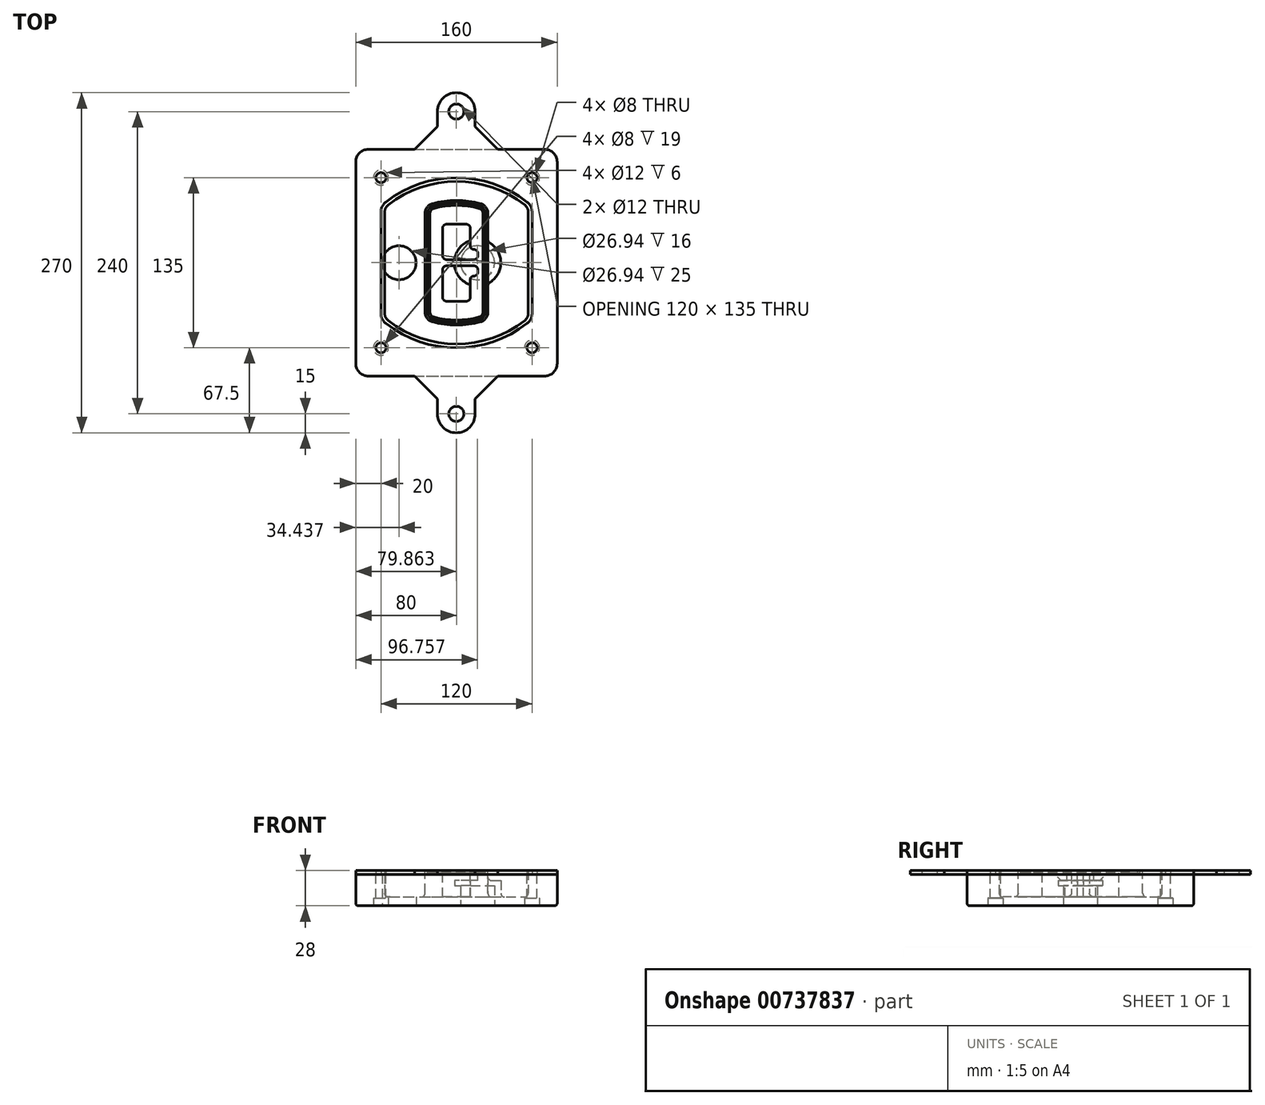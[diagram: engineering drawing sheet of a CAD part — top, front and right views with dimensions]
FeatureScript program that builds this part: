
annotation { "Feature Type Name" : "Feature", "Feature Type Description" : "" }
export const myFeature = defineFeature(function(context is Context, id is Id, definition is map)
    precondition{}
    {
        {
            var Q0;
            Q0=qCreatedBy(makeId("Top.planeOp"),FACE);
            var sketch = newSketch(context, id + "F0", { "sketchPlane" : qUnion([Q0])});
            skPoint(sketch, "E0.rect.middle", {"position": v(0, 0) * mm});
            skLineSegment(sketch, "E1.bottom", {"start": v(-70, -90) * mm, "end": v(70, -90) * mm});
            skLineSegment(sketch, "E1.top", {"start": v(-70, 90) * mm, "end": v(70, 90) * mm});
            skLineSegment(sketch, "E1.left", {"start": v(-80, -80) * mm, "end": v(-80, 80) * mm});
            skLineSegment(sketch, "E1.right", {"start": v(80, -80) * mm, "end": v(80, 80) * mm});
            skLineSegment(sketch, "E2", {"start": v(-80, 90) * mm, "end": v(80, -90) * mm, "construction": true});
            skLineSegment(sketch, "E3", {"start": v(80, 90) * mm, "end": v(-80, -90) * mm, "construction": true});
            skCircle(sketch, "E4", {"center": v(-60, 67.5) * mm, "radius": 4 * mm});
            skCircle(sketch, "E5", {"center": v(60, 67.5) * mm, "radius": 4 * mm});
            skCircle(sketch, "E6", {"center": v(60, -67.5) * mm, "radius": 4 * mm});
            skCircle(sketch, "E7", {"center": v(-60, -67.5) * mm, "radius": 4 * mm});
            skLineSegment(sketch, "E8", {"start": v(-60, 67.5) * mm, "end": v(60, 67.5) * mm, "construction": true});
            skLineSegment(sketch, "E9", {"start": v(60, 67.5) * mm, "end": v(60, -67.5) * mm, "construction": true});
            skLineSegment(sketch, "E10", {"start": v(60, -67.5) * mm, "end": v(-60, -67.5) * mm, "construction": true});
            skLineSegment(sketch, "E11", {"start": v(-60, -67.5) * mm, "end": v(-60, 67.5) * mm, "construction": true});
            skLineSegment(sketch, "E12", {"start": v(-60, 40.3) * mm, "end": v(-60, -40.3) * mm});
            skLineSegment(sketch, "E13", {"start": v(60, 40.3) * mm, "end": v(60, -40.3) * mm});
            skArc(sketch, "E14", {"start": v(56.15, 48.18) * mm, "mid": v(0, 67.5) * mm, "end": v(-56.15, 48.18) * mm});
            skArc(sketch, "E15", {"start": v(-56.15, -48.18) * mm, "mid": v(0, -67.5) * mm, "end": v(56.15, -48.18) * mm});
            skLineSegment(sketch, "E16", {"start": v(-60, 0) * mm, "end": v(60, 0) * mm, "construction": true});
            skPoint(sketch, "E17.visualSharp", {"position": v(-60, -45) * mm});
            skArc(sketch, "E17.filletArc", {"start": v(-60, -40.3) * mm, "mid": v(-58.99, -44.68) * mm, "end": v(-56.15, -48.18) * mm});
            skPoint(sketch, "E18.visualSharp", {"position": v(-60, 45) * mm});
            skArc(sketch, "E18.filletArc", {"start": v(-56.15, 48.18) * mm, "mid": v(-58.99, 44.68) * mm, "end": v(-60, 40.3) * mm});
            skPoint(sketch, "E19.visualSharp", {"position": v(60, 45) * mm});
            skArc(sketch, "E19.filletArc", {"start": v(60, 40.3) * mm, "mid": v(58.99, 44.68) * mm, "end": v(56.15, 48.18) * mm});
            skPoint(sketch, "E20.visualSharp", {"position": v(60, -45) * mm});
            skArc(sketch, "E20.filletArc", {"start": v(56.15, -48.18) * mm, "mid": v(58.99, -44.68) * mm, "end": v(60, -40.3) * mm});
            skPoint(sketch, "E21.visualSharp", {"position": v(-80, 90) * mm});
            skArc(sketch, "E21.filletArc", {"start": v(-70, 90) * mm, "mid": v(-77.07, 87.07) * mm, "end": v(-80, 80) * mm});
            skPoint(sketch, "E22.visualSharp", {"position": v(80, 90) * mm});
            skArc(sketch, "E22.filletArc", {"start": v(80, 80) * mm, "mid": v(77.07, 87.07) * mm, "end": v(70, 90) * mm});
            skPoint(sketch, "E23.visualSharp", {"position": v(80, -90) * mm});
            skArc(sketch, "E23.filletArc", {"start": v(70, -90) * mm, "mid": v(77.07, -87.07) * mm, "end": v(80, -80) * mm});
            skPoint(sketch, "E24.visualSharp", {"position": v(-80, -90) * mm});
            skArc(sketch, "E24.filletArc", {"start": v(-80, -80) * mm, "mid": v(-77.07, -87.07) * mm, "end": v(-70, -90) * mm});
            skArc(sketch, "E25.0", {"start": v(57, 40.3) * mm, "mid": v(56.3, 43.36) * mm, "end": v(54.3, 45.81) * mm});
            skLineSegment(sketch, "E25.1", {"start": v(57, 40.3) * mm, "end": v(57, -40.3) * mm});
            skArc(sketch, "E25.2", {"start": v(54.3, -45.81) * mm, "mid": v(56.3, -43.36) * mm, "end": v(57, -40.3) * mm});
            skArc(sketch, "E25.3", {"start": v(-54.3, -45.81) * mm, "mid": v(0, -64.5) * mm, "end": v(54.3, -45.81) * mm});
            skArc(sketch, "E25.4", {"start": v(-57, -40.3) * mm, "mid": v(-56.3, -43.36) * mm, "end": v(-54.3, -45.81) * mm});
            skArc(sketch, "E25.5", {"start": v(54.3, 45.81) * mm, "mid": v(0, 64.5) * mm, "end": v(-54.3, 45.81) * mm});
            skLineSegment(sketch, "E25.6", {"start": v(-57, 40.3) * mm, "end": v(-57, -40.3) * mm});
            skArc(sketch, "E25.7", {"start": v(-54.3, 45.81) * mm, "mid": v(-56.3, 43.36) * mm, "end": v(-57, 40.3) * mm});
            skArc(sketch, "E26.0", {"start": v(-58.62, 51.33) * mm, "mid": v(-62.58, 46.43) * mm, "end": v(-64, 40.3) * mm});
            skArc(sketch, "E26.1", {"start": v(58.62, 51.33) * mm, "mid": v(0, 71.5) * mm, "end": v(-58.62, 51.33) * mm});
            skArc(sketch, "E26.2", {"start": v(64, 40.3) * mm, "mid": v(62.58, 46.43) * mm, "end": v(58.62, 51.33) * mm});
            skLineSegment(sketch, "E26.3", {"start": v(64, 40.3) * mm, "end": v(64, -40.3) * mm});
            skArc(sketch, "E26.4", {"start": v(58.62, -51.33) * mm, "mid": v(62.58, -46.43) * mm, "end": v(64, -40.3) * mm});
            skLineSegment(sketch, "E26.5", {"start": v(-64, 40.3) * mm, "end": v(-64, -40.3) * mm});
            skArc(sketch, "E26.6", {"start": v(-58.62, -51.33) * mm, "mid": v(0, -71.5) * mm, "end": v(58.62, -51.33) * mm});
            skArc(sketch, "E26.7", {"start": v(-64, -40.3) * mm, "mid": v(-62.58, -46.43) * mm, "end": v(-58.62, -51.33) * mm});
            skPoint(sketch, "E27.startSnap0", {"position": v(0, 90) * mm});
            skLineSegment(sketch, "E28", {"start": v(0, 90) * mm, "end": v(0, 120) * mm, "construction": true});
            skSolve(sketch);
        }
        {
            var Q0;
            Q0=makeQuery(id+"F0.imprint","IMPRINT",FACE,{"disambiguationData":[TD([[makeQuery(id+"F0.imprint","IMPRINT",EDGE,{"derivedFrom":sQuery(id+"F0.wireOp",EDGE,"E1.bottom")}),1.0]])]});
            var Q1;
            Q1=makeQuery(id+"F0.imprint","IMPRINT",FACE,{"disambiguationData":[TD([[makeQuery(id+"F0.imprint","IMPRINT",EDGE,{"derivedFrom":sQuery(id+"F0.wireOp",EDGE,"E12")}),1.0]])]});
            var Q2;
            Q2=makeQuery(id+"F0.imprint","IMPRINT",FACE,{"disambiguationData":[TD([[makeQuery(id+"F0.imprint","IMPRINT",EDGE,{"derivedFrom":sQuery(id+"F0.wireOp",EDGE,"E25.0")}),1.0]])]});
            var Q3;
            Q3=makeQuery(id+"F0.imprint","IMPRINT",FACE,{"disambiguationData":[TD([[makeQuery(id+"F0.imprint","IMPRINT",EDGE,{"derivedFrom":sQuery(id+"F0.wireOp",EDGE,"E12")}),-1.0]])]});
            extrude(context, id + "F1", {"entities" : qUnion([Q0, Q1, Q2, Q3]), "oppositeDirection" : true, "depth" : 25 * mm});
        }
        {
            var Q0;
            Q0=makeQuery(id+"F0.imprint","IMPRINT",FACE,{"disambiguationData":[TD([[makeQuery(id+"F0.imprint","IMPRINT",EDGE,{"derivedFrom":sQuery(id+"F0.wireOp",EDGE,"E12")}),1.0]])]});
            extrude(context, id + "F2", {"entities" : qUnion([Q0]), "operationType" : NewBodyOperationType.ADD, "depth" : 3 * mm});
        }
        {
            var Q0;
            Q0=makeQuery(id+"F0.imprint","IMPRINT",FACE,{"disambiguationData":[TD([[makeQuery(id+"F0.imprint","IMPRINT",EDGE,{"derivedFrom":sQuery(id+"F0.wireOp",EDGE,"E25.0")}),1.0]])]});
            extrude(context, id + "F3", {"entities" : qUnion([Q0]), "operationType" : NewBodyOperationType.REMOVE, "oppositeDirection" : true, "depth" : 18 * mm});
        }
        {
            var Q0;
            Q0=makeQuery(id+"F2.opExtrude","CAP_FACE",FACE,{"disambiguationData":[OSD([sQuery(id+"F0.wireOp",EDGE,"E12"),sQuery(id+"F0.wireOp",EDGE,"E13"),sQuery(id+"F0.wireOp",EDGE,"E14"),sQuery(id+"F0.wireOp",EDGE,"E15"),sQuery(id+"F0.wireOp",EDGE,"E17.filletArc"),sQuery(id+"F0.wireOp",EDGE,"E18.filletArc"),sQuery(id+"F0.wireOp",EDGE,"E19.filletArc"),sQuery(id+"F0.wireOp",EDGE,"E20.filletArc"),sQuery(id+"F0.wireOp",EDGE,"E25.0"),sQuery(id+"F0.wireOp",EDGE,"E25.1"),sQuery(id+"F0.wireOp",EDGE,"E25.2"),sQuery(id+"F0.wireOp",EDGE,"E25.3"),sQuery(id+"F0.wireOp",EDGE,"E25.4"),sQuery(id+"F0.wireOp",EDGE,"E25.5"),sQuery(id+"F0.wireOp",EDGE,"E25.6"),sQuery(id+"F0.wireOp",EDGE,"E25.7")])],"isStart":false});
            var sketch = newSketch(context, id + "F4", { "sketchPlane" : qUnion([Q0])});
            skArc(sketch, "E29.0", {"start": v(-19.08, -46.97) * mm, "mid": v(0, -49.5) * mm, "end": v(19.08, -46.97) * mm});
            skArc(sketch, "E30.0", {"start": v(19.08, 46.97) * mm, "mid": v(0, 49.5) * mm, "end": v(-19.08, 46.97) * mm});
            skLineSegment(sketch, "E31", {"start": v(-25, 39.25) * mm, "end": v(-25, -39.25) * mm});
            skLineSegment(sketch, "E32", {"start": v(25, 39.25) * mm, "end": v(25, -39.25) * mm});
            skLineSegment(sketch, "E33", {"start": v(-25, 45.1) * mm, "end": v(25, 45.1) * mm, "construction": true});
            skLineSegment(sketch, "E34", {"start": v(-25, -45.1) * mm, "end": v(25, -45.1) * mm, "construction": true});
            skPoint(sketch, "E35.visualSharp", {"position": v(-25, 45.1) * mm});
            skArc(sketch, "E35.filletArc", {"start": v(-19.08, 46.97) * mm, "mid": v(-23.35, 44.11) * mm, "end": v(-25, 39.25) * mm});
            skPoint(sketch, "E36.visualSharp", {"position": v(25, 45.1) * mm});
            skArc(sketch, "E36.filletArc", {"start": v(25, 39.25) * mm, "mid": v(23.35, 44.11) * mm, "end": v(19.08, 46.97) * mm});
            skPoint(sketch, "E37.visualSharp", {"position": v(25, -45.1) * mm});
            skArc(sketch, "E37.filletArc", {"start": v(19.08, -46.97) * mm, "mid": v(23.35, -44.11) * mm, "end": v(25, -39.25) * mm});
            skPoint(sketch, "E38.visualSharp", {"position": v(-25, -45.1) * mm});
            skArc(sketch, "E38.filletArc", {"start": v(-25, -39.25) * mm, "mid": v(-23.35, -44.11) * mm, "end": v(-19.08, -46.97) * mm});
            skArc(sketch, "E39.0", {"start": v(54.3, 45.81) * mm, "mid": v(0, 64.5) * mm, "end": v(-54.3, 45.81) * mm});
            skArc(sketch, "E39.1", {"start": v(-54.3, 45.81) * mm, "mid": v(-56.3, 43.36) * mm, "end": v(-57, 40.3) * mm});
            skLineSegment(sketch, "E39.2", {"start": v(-57, 40.3) * mm, "end": v(-57, -40.3) * mm});
            skArc(sketch, "E39.3", {"start": v(-57, -40.3) * mm, "mid": v(-56.3, -43.36) * mm, "end": v(-54.3, -45.81) * mm});
            skArc(sketch, "E39.4", {"start": v(-54.3, -45.81) * mm, "mid": v(0, -64.5) * mm, "end": v(54.3, -45.81) * mm});
            skArc(sketch, "E39.5", {"start": v(54.3, -45.81) * mm, "mid": v(56.3, -43.36) * mm, "end": v(57, -40.3) * mm});
            skLineSegment(sketch, "E39.6", {"start": v(57, 40.3) * mm, "end": v(57, -40.3) * mm});
            skArc(sketch, "E39.7", {"start": v(57, 40.3) * mm, "mid": v(56.3, 43.36) * mm, "end": v(54.3, 45.81) * mm});
            skLineSegment(sketch, "E40.0", {"start": v(23, 39.25) * mm, "end": v(23, -39.25) * mm});
            skArc(sketch, "E40.1", {"start": v(18.56, -45.04) * mm, "mid": v(21.76, -42.9) * mm, "end": v(23, -39.25) * mm});
            skArc(sketch, "E40.2", {"start": v(-18.56, -45.04) * mm, "mid": v(0, -47.5) * mm, "end": v(18.56, -45.04) * mm});
            skArc(sketch, "E40.3", {"start": v(-23, -39.25) * mm, "mid": v(-21.76, -42.9) * mm, "end": v(-18.56, -45.04) * mm});
            skLineSegment(sketch, "E40.4", {"start": v(-23, 39.25) * mm, "end": v(-23, -39.25) * mm});
            skArc(sketch, "E40.5", {"start": v(23, 39.25) * mm, "mid": v(21.76, 42.9) * mm, "end": v(18.56, 45.04) * mm});
            skArc(sketch, "E40.6", {"start": v(-18.56, 45.04) * mm, "mid": v(-21.76, 42.9) * mm, "end": v(-23, 39.25) * mm});
            skArc(sketch, "E40.7", {"start": v(18.56, 45.04) * mm, "mid": v(0, 47.5) * mm, "end": v(-18.56, 45.04) * mm});
            skArc(sketch, "E41.0", {"start": v(21, 39.25) * mm, "mid": v(20.18, 41.68) * mm, "end": v(18.04, 43.1) * mm});
            skLineSegment(sketch, "E41.1", {"start": v(21, 39.25) * mm, "end": v(21, -39.25) * mm});
            skArc(sketch, "E41.2", {"start": v(18.04, -43.1) * mm, "mid": v(20.18, -41.68) * mm, "end": v(21, -39.25) * mm});
            skArc(sketch, "E41.3", {"start": v(-18.04, -43.1) * mm, "mid": v(0, -45.5) * mm, "end": v(18.04, -43.1) * mm});
            skArc(sketch, "E41.4", {"start": v(-21, -39.25) * mm, "mid": v(-20.18, -41.68) * mm, "end": v(-18.04, -43.1) * mm});
            skArc(sketch, "E41.5", {"start": v(18.04, 43.1) * mm, "mid": v(0, 45.5) * mm, "end": v(-18.04, 43.1) * mm});
            skLineSegment(sketch, "E41.6", {"start": v(-21, 39.25) * mm, "end": v(-21, -39.25) * mm});
            skArc(sketch, "E41.7", {"start": v(-18.04, 43.1) * mm, "mid": v(-20.18, 41.68) * mm, "end": v(-21, 39.25) * mm});
            skLineSegment(sketch, "E42", {"start": v(-25, 0) * mm, "end": v(25, 0) * mm, "construction": true});
            skLineSegment(sketch, "E43", {"start": v(-11, 5.5) * mm, "end": v(-11, 27.5) * mm});
            skLineSegment(sketch, "E44", {"start": v(-8, 30.5) * mm, "end": v(8, 30.5) * mm});
            skLineSegment(sketch, "E45", {"start": v(11, 27.5) * mm, "end": v(11, 13.5) * mm});
            skLineSegment(sketch, "E46", {"start": v(14, 10.5) * mm, "end": v(14, 10.5) * mm});
            skLineSegment(sketch, "E47", {"start": v(17, 7.5) * mm, "end": v(17, 5.5) * mm});
            skLineSegment(sketch, "E48", {"start": v(14, 2.5) * mm, "end": v(-8, 2.5) * mm});
            skPoint(sketch, "E49.visualSharp", {"position": v(-11, 30.5) * mm});
            skArc(sketch, "E49.filletArc", {"start": v(-8, 30.5) * mm, "mid": v(-10.12, 29.62) * mm, "end": v(-11, 27.5) * mm});
            skPoint(sketch, "E50.visualSharp", {"position": v(11, 30.5) * mm});
            skArc(sketch, "E50.filletArc", {"start": v(11, 27.5) * mm, "mid": v(10.12, 29.62) * mm, "end": v(8, 30.5) * mm});
            skPoint(sketch, "E51.visualSharp", {"position": v(11, 10.5) * mm});
            skArc(sketch, "E51.filletArc", {"start": v(11, 13.5) * mm, "mid": v(11.88, 11.38) * mm, "end": v(14, 10.5) * mm});
            skPoint(sketch, "E52.visualSharp", {"position": v(17, 10.5) * mm});
            skArc(sketch, "E52.filletArc", {"start": v(17, 7.5) * mm, "mid": v(16.12, 9.62) * mm, "end": v(14, 10.5) * mm});
            skPoint(sketch, "E53.visualSharp", {"position": v(17, 2.5) * mm});
            skArc(sketch, "E53.filletArc", {"start": v(14, 2.5) * mm, "mid": v(16.12, 3.38) * mm, "end": v(17, 5.5) * mm});
            skPoint(sketch, "E54.visualSharp", {"position": v(-11, 2.5) * mm});
            skArc(sketch, "E54.filletArc", {"start": v(-11, 5.5) * mm, "mid": v(-10.12, 3.38) * mm, "end": v(-8, 2.5) * mm});
            skLineSegment(sketch, "E55.0.MirrorCS", {"start": v(14, -2.5) * mm, "end": v(-8, -2.5) * mm});
            skArc(sketch, "E56.0.MirrorCS", {"start": v(-11, -5.5) * mm, "mid": v(-10.12, -3.38) * mm, "end": v(-8, -2.5) * mm});
            skLineSegment(sketch, "E57.0.MirrorCS", {"start": v(-11, -5.5) * mm, "end": v(-11, -27.5) * mm});
            skArc(sketch, "E58.0.MirrorCS", {"start": v(-8, -30.5) * mm, "mid": v(-10.12, -29.62) * mm, "end": v(-11, -27.5) * mm});
            skLineSegment(sketch, "E59.0.MirrorCS", {"start": v(-8, -30.5) * mm, "end": v(8, -30.5) * mm});
            skArc(sketch, "E60.0.MirrorCS", {"start": v(11, -27.5) * mm, "mid": v(10.12, -29.62) * mm, "end": v(8, -30.5) * mm});
            skLineSegment(sketch, "E61.0.MirrorCS", {"start": v(11, -27.5) * mm, "end": v(11, -13.5) * mm});
            skArc(sketch, "E62.0.MirrorCS", {"start": v(11, -13.5) * mm, "mid": v(11.88, -11.38) * mm, "end": v(14, -10.5) * mm});
            skArc(sketch, "E63.0.MirrorCS", {"start": v(17, -7.5) * mm, "mid": v(16.12, -9.62) * mm, "end": v(14, -10.5) * mm});
            skLineSegment(sketch, "E64.0.MirrorCS", {"start": v(17, -7.5) * mm, "end": v(17, -5.5) * mm});
            skArc(sketch, "E65.0.MirrorCS", {"start": v(14, -2.5) * mm, "mid": v(16.12, -3.38) * mm, "end": v(17, -5.5) * mm});
            skSolve(sketch);
        }
        {
            var Q0;
            Q0=makeQuery(id+"F4.imprint","IMPRINT",FACE,{"disambiguationData":[TD([[makeQuery(id+"F4.imprint","IMPRINT",EDGE,{"derivedFrom":sQuery(id+"F4.wireOp",EDGE,"E29.0")}),1.0]])]});
            var Q1;
            Q1=makeQuery(id+"F4.imprint","IMPRINT",FACE,{"disambiguationData":[TD([[makeQuery(id+"F4.imprint","IMPRINT",EDGE,{"derivedFrom":sQuery(id+"F4.wireOp",EDGE,"E40.0")}),-1.0]])]});
            var Q2;
            Q2=makeQuery(id+"F4.imprint","IMPRINT",FACE,{"disambiguationData":[TD([[makeQuery(id+"F4.imprint","IMPRINT",EDGE,{"derivedFrom":sQuery(id+"F4.wireOp",EDGE,"E41.0")}),1.0]])]});
            extrude(context, id + "F5", {"entities" : qUnion([Q0, Q1, Q2]), "operationType" : NewBodyOperationType.ADD, "endBound" : BoundingType.UP_TO_NEXT, "oppositeDirection" : true, "depth" : 25 * mm});
        }
        {
            var Q0;
            Q0=makeQuery(id+"F4.imprint","IMPRINT",FACE,{"disambiguationData":[TD([[makeQuery(id+"F4.imprint","IMPRINT",EDGE,{"derivedFrom":sQuery(id+"F4.wireOp",EDGE,"E40.0")}),-1.0]])]});
            extrude(context, id + "F6", {"entities" : qUnion([Q0]), "operationType" : NewBodyOperationType.REMOVE, "oppositeDirection" : true, "depth" : 2 * mm});
        }
        {
            var Q0;
            Q0=makeQuery(id+"F1.opExtrude","CAP_FACE",FACE,{"disambiguationData":[OSD([sQuery(id+"F0.wireOp",EDGE,"E1.bottom"),sQuery(id+"F0.wireOp",EDGE,"E1.top"),sQuery(id+"F0.wireOp",EDGE,"E1.left"),sQuery(id+"F0.wireOp",EDGE,"E1.right"),sQuery(id+"F0.wireOp",EDGE,"E4"),sQuery(id+"F0.wireOp",EDGE,"E5"),sQuery(id+"F0.wireOp",EDGE,"E6"),sQuery(id+"F0.wireOp",EDGE,"E7"),sQuery(id+"F0.wireOp",EDGE,"E21.filletArc"),sQuery(id+"F0.wireOp",EDGE,"E22.filletArc"),sQuery(id+"F0.wireOp",EDGE,"E23.filletArc"),sQuery(id+"F0.wireOp",EDGE,"E24.filletArc")])],"isStart":false});
            var sketch = newSketch(context, id + "F7", { "sketchPlane" : qUnion([Q0])});
            skCircle(sketch, "E66", {"center": v(16.76, 0) * mm, "radius": 13.47 * mm});
            skCircle(sketch, "E67", {"center": v(-45.56, 0) * mm, "radius": 13.47 * mm});
            skLineSegment(sketch, "E68", {"start": v(80, 0) * mm, "end": v(-80, 0) * mm});
            skCircle(sketch, "E69", {"center": v(16.76, 0) * mm, "radius": 18.47 * mm});
            skCircle(sketch, "E70", {"center": v(60, -67.5) * mm, "radius": 6 * mm});
            skCircle(sketch, "E71", {"center": v(-60, -67.5) * mm, "radius": 6 * mm});
            skCircle(sketch, "E72", {"center": v(-60, 67.5) * mm, "radius": 6 * mm});
            skCircle(sketch, "E73", {"center": v(60, 67.5) * mm, "radius": 6 * mm});
            skSolve(sketch);
        }
        {
            var Q0;
            {var subQ1=sQuery(id+"F7.wireOp",EDGE,"E68");var subQ4=sQuery(id+"F7.wireOp",EDGE,"E66");var subQ6=makeQuery(id+"F7.imprint","INTERSECT",VERTEX,{"disambiguationData":[OD(0.0)],"derivedFrom":[subQ4,subQ1]});Q0=makeQuery(id+"F7.imprint","IMPRINT",FACE,{"disambiguationData":[TD([[makeQuery(id+"F7.imprint","IMPRINT",EDGE,{"disambiguationData":[TD([[subQ6,-1.0]])],"derivedFrom":subQ4}),-1.0]])]});}
            var Q1;
            {var subQ0=sQuery(id+"F7.wireOp",EDGE,"E68");var subQ1=sQuery(id+"F7.wireOp",EDGE,"E66");var subQ3=makeQuery(id+"F7.imprint","INTERSECT",VERTEX,{"disambiguationData":[OD(0.0)],"derivedFrom":[subQ1,subQ0]});Q1=makeQuery(id+"F7.imprint","IMPRINT",FACE,{"disambiguationData":[TD([[makeQuery(id+"F7.imprint","IMPRINT",EDGE,{"disambiguationData":[TD([[subQ3,-1.0]])],"derivedFrom":subQ1}),1.0]])]});}
            var Q2;
            {var subQ0=sQuery(id+"F7.wireOp",EDGE,"E68");var subQ1=sQuery(id+"F7.wireOp",EDGE,"E66");var subQ3=makeQuery(id+"F7.imprint","INTERSECT",VERTEX,{"disambiguationData":[OD(0.0)],"derivedFrom":[subQ1,subQ0]});Q2=makeQuery(id+"F7.imprint","IMPRINT",FACE,{"disambiguationData":[TD([[makeQuery(id+"F7.imprint","IMPRINT",EDGE,{"disambiguationData":[TD([[subQ3,1.0]])],"derivedFrom":subQ1}),1.0]])]});}
            var Q3;
            {var subQ1=sQuery(id+"F7.wireOp",EDGE,"E68");var subQ4=sQuery(id+"F7.wireOp",EDGE,"E66");var subQ6=makeQuery(id+"F7.imprint","INTERSECT",VERTEX,{"disambiguationData":[OD(0.0)],"derivedFrom":[subQ4,subQ1]});Q3=makeQuery(id+"F7.imprint","IMPRINT",FACE,{"disambiguationData":[TD([[makeQuery(id+"F7.imprint","IMPRINT",EDGE,{"disambiguationData":[TD([[subQ6,1.0]])],"derivedFrom":subQ4}),-1.0]])]});}
            extrude(context, id + "F8", {"entities" : qUnion([Q0, Q1, Q2, Q3]), "operationType" : NewBodyOperationType.ADD, "oppositeDirection" : true, "depth" : 20 * mm});
        }
        {
            var Q0;
            {var subQ0=sQuery(id+"F7.wireOp",EDGE,"E68");var subQ1=sQuery(id+"F7.wireOp",EDGE,"E66");var subQ3=makeQuery(id+"F7.imprint","INTERSECT",VERTEX,{"disambiguationData":[OD(0.0)],"derivedFrom":[subQ1,subQ0]});Q0=makeQuery(id+"F7.imprint","IMPRINT",FACE,{"disambiguationData":[TD([[makeQuery(id+"F7.imprint","IMPRINT",EDGE,{"disambiguationData":[TD([[subQ3,-1.0]])],"derivedFrom":subQ1}),1.0]])]});}
            var Q1;
            {var subQ0=sQuery(id+"F7.wireOp",EDGE,"E68");var subQ1=sQuery(id+"F7.wireOp",EDGE,"E66");var subQ3=makeQuery(id+"F7.imprint","INTERSECT",VERTEX,{"disambiguationData":[OD(0.0)],"derivedFrom":[subQ1,subQ0]});Q1=makeQuery(id+"F7.imprint","IMPRINT",FACE,{"disambiguationData":[TD([[makeQuery(id+"F7.imprint","IMPRINT",EDGE,{"disambiguationData":[TD([[subQ3,1.0]])],"derivedFrom":subQ1}),1.0]])]});}
            extrude(context, id + "F9", {"entities" : qUnion([Q0, Q1]), "operationType" : NewBodyOperationType.REMOVE, "oppositeDirection" : true, "depth" : 16 * mm});
        }
        {
            var Q0;
            {var subQ0=sQuery(id+"F7.wireOp",EDGE,"E68");var subQ1=sQuery(id+"F7.wireOp",EDGE,"E67");var subQ3=makeQuery(id+"F7.imprint","INTERSECT",VERTEX,{"disambiguationData":[OD(0.0)],"derivedFrom":[subQ1,subQ0]});Q0=makeQuery(id+"F7.imprint","IMPRINT",FACE,{"disambiguationData":[TD([[makeQuery(id+"F7.imprint","IMPRINT",EDGE,{"disambiguationData":[TD([[subQ3,-1.0]])],"derivedFrom":subQ1}),1.0]])]});}
            var Q1;
            {var subQ0=sQuery(id+"F7.wireOp",EDGE,"E68");var subQ1=sQuery(id+"F7.wireOp",EDGE,"E67");var subQ3=makeQuery(id+"F7.imprint","INTERSECT",VERTEX,{"disambiguationData":[OD(0.0)],"derivedFrom":[subQ1,subQ0]});Q1=makeQuery(id+"F7.imprint","IMPRINT",FACE,{"disambiguationData":[TD([[makeQuery(id+"F7.imprint","IMPRINT",EDGE,{"disambiguationData":[TD([[subQ3,1.0]])],"derivedFrom":subQ1}),1.0]])]});}
            extrude(context, id + "F10", {"entities" : qUnion([Q0, Q1]), "operationType" : NewBodyOperationType.REMOVE, "oppositeDirection" : true, "depth" : 25 * mm});
        }
        {
            var Q0;
            Q0=makeQuery(id+"F7.imprint","IMPRINT",FACE,{"disambiguationData":[TD([[makeQuery(id+"F7.imprint","IMPRINT",EDGE,{"derivedFrom":sQuery(id+"F7.wireOp",EDGE,"E70")}),1.0]])]});
            var Q1;
            Q1=makeQuery(id+"F7.imprint","IMPRINT",FACE,{"disambiguationData":[TD([[makeQuery(id+"F7.imprint","IMPRINT",EDGE,{"derivedFrom":makeQuery(id+"F1.opExtrude","CAP_EDGE",EDGE,{"disambiguationData":[OSD([sQuery(id+"F0.wireOp",EDGE,"E5")])],"isStart":false})}),-1.0]])]});
            var Q2;
            Q2=makeQuery(id+"F7.imprint","IMPRINT",FACE,{"disambiguationData":[TD([[makeQuery(id+"F7.imprint","IMPRINT",EDGE,{"derivedFrom":sQuery(id+"F7.wireOp",EDGE,"E71")}),1.0]])]});
            var Q3;
            Q3=makeQuery(id+"F7.imprint","IMPRINT",FACE,{"disambiguationData":[TD([[makeQuery(id+"F7.imprint","IMPRINT",EDGE,{"derivedFrom":makeQuery(id+"F1.opExtrude","CAP_EDGE",EDGE,{"disambiguationData":[OSD([sQuery(id+"F0.wireOp",EDGE,"E4")])],"isStart":false})}),-1.0]])]});
            var Q4;
            Q4=makeQuery(id+"F7.imprint","IMPRINT",FACE,{"disambiguationData":[TD([[makeQuery(id+"F7.imprint","IMPRINT",EDGE,{"derivedFrom":sQuery(id+"F7.wireOp",EDGE,"E72")}),1.0]])]});
            var Q5;
            Q5=makeQuery(id+"F7.imprint","IMPRINT",FACE,{"disambiguationData":[TD([[makeQuery(id+"F7.imprint","IMPRINT",EDGE,{"derivedFrom":makeQuery(id+"F1.opExtrude","CAP_EDGE",EDGE,{"disambiguationData":[OSD([sQuery(id+"F0.wireOp",EDGE,"E7")])],"isStart":false})}),-1.0]])]});
            var Q6;
            Q6=makeQuery(id+"F7.imprint","IMPRINT",FACE,{"disambiguationData":[TD([[makeQuery(id+"F7.imprint","IMPRINT",EDGE,{"derivedFrom":sQuery(id+"F7.wireOp",EDGE,"E73")}),1.0]])]});
            var Q7;
            Q7=makeQuery(id+"F7.imprint","IMPRINT",FACE,{"disambiguationData":[TD([[makeQuery(id+"F7.imprint","IMPRINT",EDGE,{"derivedFrom":makeQuery(id+"F1.opExtrude","CAP_EDGE",EDGE,{"disambiguationData":[OSD([sQuery(id+"F0.wireOp",EDGE,"E6")])],"isStart":false})}),-1.0]])]});
            extrude(context, id + "F11", {"entities" : qUnion([Q0, Q1, Q2, Q3, Q4, Q5, Q6, Q7]), "operationType" : NewBodyOperationType.REMOVE, "oppositeDirection" : true, "depth" : 6 * mm});
        }
        {
            var Q0;
            Q0=makeQuery(id+"F9.boolean.opBoolean","COPY",FACE,{"derivedFrom":makeQuery(id+"F9.opExtrude","CAP_FACE",FACE,{"disambiguationData":[OSD([sQuery(id+"F7.wireOp",EDGE,"E66")])],"isStart":false})});
            var sketch = newSketch(context, id + "F12", { "sketchPlane" : qUnion([Q0])});
            skArc(sketch, "E74.0", {"start": v(11, 17.55) * mm, "mid": v(2.57, 11.82) * mm, "end": v(-1.54, 2.5) * mm});
            skArc(sketch, "E74.1", {"start": v(-1.54, -2.5) * mm, "mid": v(2.57, -11.82) * mm, "end": v(11, -17.55) * mm});
            skLineSegment(sketch, "E75", {"start": v(-1.54, -2.5) * mm, "end": v(14, -2.5) * mm});
            skLineSegment(sketch, "E76.0", {"start": v(14, 2.5) * mm, "end": v(-1.54, 2.5) * mm});
            skArc(sketch, "E76.1", {"start": v(14, 2.5) * mm, "mid": v(16.12, 3.38) * mm, "end": v(17, 5.5) * mm});
            skLineSegment(sketch, "E76.2", {"start": v(17, 7.5) * mm, "end": v(17, 5.5) * mm});
            skArc(sketch, "E76.3", {"start": v(17, 7.5) * mm, "mid": v(16.12, 9.62) * mm, "end": v(14, 10.5) * mm});
            skArc(sketch, "E76.4", {"start": v(11, 13.5) * mm, "mid": v(11.88, 11.38) * mm, "end": v(14, 10.5) * mm});
            skLineSegment(sketch, "E76.5", {"start": v(11, 17.55) * mm, "end": v(11, 13.5) * mm});
            skLineSegment(sketch, "E76.7", {"start": v(14, -2.5) * mm, "end": v(-1.54, -2.5) * mm});
            skArc(sketch, "E76.8", {"start": v(14, -2.5) * mm, "mid": v(16.12, -3.38) * mm, "end": v(17, -5.5) * mm});
            skLineSegment(sketch, "E76.9", {"start": v(17, -7.5) * mm, "end": v(17, -5.5) * mm});
            skArc(sketch, "E76.10", {"start": v(17, -7.5) * mm, "mid": v(16.12, -9.62) * mm, "end": v(14, -10.5) * mm});
            skArc(sketch, "E76.11", {"start": v(11, -13.5) * mm, "mid": v(11.88, -11.38) * mm, "end": v(14, -10.5) * mm});
            skLineSegment(sketch, "E76.12", {"start": v(11, -17.55) * mm, "end": v(11, -13.5) * mm});
            skPoint(sketch, "E77.orphan", {"position": v(11, -27.5) * mm});
            skPoint(sketch, "E78.orphan", {"position": v(-8, -2.5) * mm});
            skPoint(sketch, "E79.orphan", {"position": v(-8, 2.5) * mm});
            skPoint(sketch, "E80.orphan", {"position": v(11, 27.5) * mm});
            skSolve(sketch);
        }
        {
            var Q0;
            {var subQ7=sQuery(id+"F12.wireOp",EDGE,"E74.0");var subQ14=sQuery(id+"F12.wireOp",EDGE,"E74.1");var subQ16=sQuery(id+"F12.wireOp",EDGE,"E76.1");var subQ18=sQuery(id+"F12.wireOp",EDGE,"E76.8");Q0=qUnion([makeQuery(id+"F12.imprint","IMPRINT",FACE,{"disambiguationData":[TD([[makeQuery(id+"F12.imprint","IMPRINT",EDGE,{"derivedFrom":subQ7}),1.0]])]}),makeQuery(id+"F12.imprint","IMPRINT",FACE,{"disambiguationData":[TD([[makeQuery(id+"F12.imprint","IMPRINT",EDGE,{"derivedFrom":subQ14}),1.0]])]}),makeQuery(id+"F12.imprint","IMPRINT",FACE,{"disambiguationData":[TD([[makeQuery(id+"F12.imprint","IMPRINT",EDGE,{"derivedFrom":subQ16}),1.0]])]}),makeQuery(id+"F12.imprint","IMPRINT",FACE,{"disambiguationData":[TD([[makeQuery(id+"F12.imprint","IMPRINT",EDGE,{"derivedFrom":subQ18}),-1.0]])]})]);}
            var Q1;
            Q1=makeQuery(id+"F5.boolean.opBoolean","SPLIT",FACE,{"disambiguationData":[TD([makeQuery(id+"F5.opExtrude","SWEPT_FACE",FACE,{"disambiguationData":[OSD([sQuery(id+"F4.wireOp",EDGE,"E43")])]})])],"derivedFrom":makeQuery(id+"F3.boolean.opBoolean","COPY",FACE,{"derivedFrom":makeQuery(id+"F3.opExtrude","CAP_FACE",FACE,{"disambiguationData":[OSD([sQuery(id+"F0.wireOp",EDGE,"E25.0"),sQuery(id+"F0.wireOp",EDGE,"E25.1"),sQuery(id+"F0.wireOp",EDGE,"E25.2"),sQuery(id+"F0.wireOp",EDGE,"E25.3"),sQuery(id+"F0.wireOp",EDGE,"E25.4"),sQuery(id+"F0.wireOp",EDGE,"E25.5"),sQuery(id+"F0.wireOp",EDGE,"E25.6"),sQuery(id+"F0.wireOp",EDGE,"E25.7")])],"isStart":false})})});
            extrude(context, id + "F13", {"entities" : qUnion([Q0]), "operationType" : NewBodyOperationType.REMOVE, "endBound" : BoundingType.UP_TO_SURFACE, "endBoundEntityFace" : qUnion([Q1]), "depth" : 25 * mm});
        }
        {
            var Q0;
            Q0=makeQuery(id+"F3.boolean.opBoolean","COPY",EDGE,{"derivedFrom":makeQuery(id+"F3.opExtrude","CAP_EDGE",EDGE,{"disambiguationData":[OSD([sQuery(id+"F0.wireOp",EDGE,"E25.6")])],"isStart":false})});
            var Q1;
            Q1=makeQuery(id+"F8.boolean.opBoolean","INTERSECT",EDGE,{"derivedFrom":[makeQuery(id+"F5.opExtrude","SWEPT_FACE",FACE,{"disambiguationData":[OSD([sQuery(id+"F4.wireOp",EDGE,"E32")])]}),makeQuery(id+"F8.opExtrude","CAP_FACE",FACE,{"disambiguationData":[OSD([sQuery(id+"F7.wireOp",EDGE,"E69")])],"isStart":false})]});
            var Q2;
            Q2=makeQuery(id+"F8.boolean.opBoolean","INTERSECT",EDGE,{"disambiguationData":[OD(1.0)],"derivedFrom":[makeQuery(id+"F5.opExtrude","SWEPT_FACE",FACE,{"disambiguationData":[OSD([sQuery(id+"F4.wireOp",EDGE,"E32")])]}),makeQuery(id+"F8.opExtrude","SWEPT_FACE",FACE,{"disambiguationData":[OSD([sQuery(id+"F7.wireOp",EDGE,"E69")])]})]});
            var Q3;
            {var subQ0=sQuery(id+"F4.wireOp",EDGE,"E32");Q3=makeQuery(id+"F8.boolean.opBoolean","SPLIT",EDGE,{"disambiguationData":[TD([makeQuery(id+"F5.opExtrude","SWEPT_FACE",FACE,{"disambiguationData":[OSD([sQuery(id+"F4.wireOp",EDGE,"E37.filletArc")])]})])],"derivedFrom":makeQuery(id+"F5.opExtrude","CAP_EDGE",EDGE,{"disambiguationData":[OSD([subQ0])],"isStart":false})});}
            var Q4;
            {var subQ0=sQuery(id+"F0.wireOp",EDGE,"E25.7");var subQ1=sQuery(id+"F0.wireOp",EDGE,"E25.1");var subQ2=sQuery(id+"F0.wireOp",EDGE,"E25.6");var subQ3=sQuery(id+"F0.wireOp",EDGE,"E25.5");var subQ4=sQuery(id+"F0.wireOp",EDGE,"E25.4");var subQ5=sQuery(id+"F0.wireOp",EDGE,"E25.0");var subQ6=sQuery(id+"F0.wireOp",EDGE,"E25.2");var subQ7=sQuery(id+"F0.wireOp",EDGE,"E25.3");Q4=makeQuery(id+"F8.boolean.opBoolean","INTERSECT",EDGE,{"derivedFrom":[makeQuery(id+"F5.boolean.opBoolean","SPLIT",FACE,{"disambiguationData":[TD([makeQuery(id+"F2.opExtrude","SWEPT_FACE",FACE,{"disambiguationData":[OSD([subQ5])]})])],"derivedFrom":makeQuery(id+"F3.boolean.opBoolean","COPY",FACE,{"derivedFrom":makeQuery(id+"F3.opExtrude","CAP_FACE",FACE,{"disambiguationData":[OSD([subQ5,subQ1,subQ6,subQ7,subQ4,subQ3,subQ2,subQ0])],"isStart":false})})}),makeQuery(id+"F8.opExtrude","SWEPT_FACE",FACE,{"disambiguationData":[OSD([sQuery(id+"F7.wireOp",EDGE,"E69")])]})]});}
            var Q5;
            Q5=makeQuery(id+"F8.boolean.opBoolean","INTERSECT",EDGE,{"disambiguationData":[OD(0.0)],"derivedFrom":[makeQuery(id+"F5.opExtrude","SWEPT_FACE",FACE,{"disambiguationData":[OSD([sQuery(id+"F4.wireOp",EDGE,"E32")])]}),makeQuery(id+"F8.opExtrude","SWEPT_FACE",FACE,{"disambiguationData":[OSD([sQuery(id+"F7.wireOp",EDGE,"E69")])]})]});
            fillet(context, id + "F14", {"entities" : qUnion([Q0, Q1, Q2, Q3, Q4, Q5]), "radius" : 3 * mm, "tangentPropagation" : true, "allowEdgeOverflow" : false});
        }
        {
            var Q0;
            Q0=makeQuery(id+"F1.opExtrude","CAP_EDGE",EDGE,{"disambiguationData":[OSD([sQuery(id+"F0.wireOp",EDGE,"E1.bottom")])],"isStart":false});
            fillet(context, id + "F15", {"entities" : qUnion([Q0]), "radius" : 2 * mm, "tangentPropagation" : true, "allowEdgeOverflow" : false});
        }
        {
            var Q0;
            {var subQ0=sQuery(id+"F0.wireOp",EDGE,"E21.filletArc");var subQ1=sQuery(id+"F0.wireOp",EDGE,"E7");var subQ2=sQuery(id+"F0.wireOp",EDGE,"E6");var subQ3=sQuery(id+"F0.wireOp",EDGE,"E5");var subQ4=sQuery(id+"F0.wireOp",EDGE,"E4");var subQ5=sQuery(id+"F0.wireOp",EDGE,"E22.filletArc");var subQ6=sQuery(id+"F0.wireOp",EDGE,"E1.bottom");var subQ7=sQuery(id+"F0.wireOp",EDGE,"E1.right");var subQ8=sQuery(id+"F0.wireOp",EDGE,"E1.top");var subQ9=sQuery(id+"F0.wireOp",EDGE,"E1.left");var subQ10=sQuery(id+"F0.wireOp",EDGE,"E23.filletArc");var subQ11=sQuery(id+"F0.wireOp",EDGE,"E24.filletArc");Q0=makeQuery(id+"F2.boolean.opBoolean","SPLIT",FACE,{"disambiguationData":[TD([makeQuery(id+"F1.opExtrude","SWEPT_FACE",FACE,{"disambiguationData":[OSD([subQ6])]})])],"derivedFrom":makeQuery(id+"F1.opExtrude","CAP_FACE",FACE,{"disambiguationData":[OSD([subQ6,subQ8,subQ9,subQ7,subQ4,subQ3,subQ2,subQ1,subQ0,subQ5,subQ10,subQ11])],"isStart":true})});}
            var sketch = newSketch(context, id + "F16", { "sketchPlane" : qUnion([Q0])});
            skPoint(sketch, "E81.0", {"position": v(-77.07, 87.07) * mm});
            skLineSegment(sketch, "E82.0", {"start": v(-70, 90) * mm, "end": v(70, 90) * mm});
            skArc(sketch, "E82.1", {"start": v(80, 80) * mm, "mid": v(77.07, 87.07) * mm, "end": v(70, 90) * mm});
            skLineSegment(sketch, "E82.2", {"start": v(80, -80) * mm, "end": v(80, 80) * mm});
            skCircle(sketch, "E82.3", {"center": v(60, 67.5) * mm, "radius": 4 * mm});
            skArc(sketch, "E82.4", {"start": v(56.15, 48.18) * mm, "mid": v(0, 67.5) * mm, "end": v(-56.15, 48.18) * mm});
            skCircle(sketch, "E82.5", {"center": v(-60, 67.5) * mm, "radius": 4 * mm});
            skArc(sketch, "E82.6", {"start": v(-70, 90) * mm, "mid": v(-77.07, 87.07) * mm, "end": v(-80, 80) * mm});
            skLineSegment(sketch, "E82.7", {"start": v(-80, -80) * mm, "end": v(-80, 80) * mm});
            skArc(sketch, "E82.8", {"start": v(-80, -80) * mm, "mid": v(-77.07, -87.07) * mm, "end": v(-70, -90) * mm});
            skLineSegment(sketch, "E82.9", {"start": v(-70, -90) * mm, "end": v(70, -90) * mm});
            skArc(sketch, "E82.10", {"start": v(70, -90) * mm, "mid": v(77.07, -87.07) * mm, "end": v(80, -80) * mm});
            skCircle(sketch, "E82.11", {"center": v(60, -67.5) * mm, "radius": 4 * mm});
            skCircle(sketch, "E82.12", {"center": v(-60, -67.5) * mm, "radius": 4 * mm});
            skArc(sketch, "E82.13", {"start": v(-56.15, -48.18) * mm, "mid": v(0, -67.5) * mm, "end": v(56.15, -48.18) * mm});
            skArc(sketch, "E82.14", {"start": v(-60, -40.3) * mm, "mid": v(-58.99, -44.68) * mm, "end": v(-56.15, -48.18) * mm});
            skLineSegment(sketch, "E82.15", {"start": v(-60, 40.3) * mm, "end": v(-60, -40.3) * mm});
            skArc(sketch, "E82.16", {"start": v(56.15, -48.18) * mm, "mid": v(58.99, -44.68) * mm, "end": v(60, -40.3) * mm});
            skLineSegment(sketch, "E82.17", {"start": v(60, 40.3) * mm, "end": v(60, -40.3) * mm});
            skArc(sketch, "E82.18", {"start": v(60, 40.3) * mm, "mid": v(58.99, 44.68) * mm, "end": v(56.15, 48.18) * mm});
            skArc(sketch, "E82.19", {"start": v(-56.15, 48.18) * mm, "mid": v(-58.99, 44.68) * mm, "end": v(-60, 40.3) * mm});
            skPoint(sketch, "E83.endSnap0", {"position": v(80, 0) * mm});
            skLineSegment(sketch, "E84", {"start": v(0, 90) * mm, "end": v(0, 120) * mm, "construction": true});
            skLineSegment(sketch, "E85", {"start": v(-33.14, 90) * mm, "end": v(-15.14, 108) * mm});
            skLineSegment(sketch, "E86", {"start": v(32.86, 90) * mm, "end": v(14.86, 108) * mm});
            skLineSegment(sketch, "E87", {"start": v(-15.14, 108) * mm, "end": v(-15.14, 120) * mm});
            skLineSegment(sketch, "E88", {"start": v(14.86, 108) * mm, "end": v(14.86, 120) * mm});
            skArc(sketch, "E89", {"start": v(14.86, 120) * mm, "mid": v(-0.14, 135) * mm, "end": v(-15.14, 120) * mm});
            skCircle(sketch, "E90", {"center": v(-0.14, 120) * mm, "radius": 6 * mm});
            skLineSegment(sketch, "E91", {"start": v(80, 0) * mm, "end": v(-80, 0) * mm, "construction": true});
            skLineSegment(sketch, "E92.MirrorCS", {"start": v(14.86, -108) * mm, "end": v(14.86, -120) * mm});
            skLineSegment(sketch, "E93.MirrorCS", {"start": v(-33.14, -90) * mm, "end": v(-15.14, -108) * mm});
            skLineSegment(sketch, "E94.MirrorCS", {"start": v(-15.14, -108) * mm, "end": v(-15.14, -120) * mm});
            skLineSegment(sketch, "E95.MirrorCS", {"start": v(32.86, -90) * mm, "end": v(14.86, -108) * mm});
            skCircle(sketch, "E96.MirrorC", {"center": v(-0.14, -120) * mm, "radius": 6 * mm});
            skArc(sketch, "E97.MirrorCS", {"start": v(14.86, -120) * mm, "mid": v(-0.14, -135) * mm, "end": v(-15.14, -120) * mm});
            skLineSegment(sketch, "E98.MirrorCS", {"start": v(0, -90) * mm, "end": v(0, -120) * mm, "construction": true});
            skSolve(sketch);
        }
        {
            var Q0;
            {var subQ0=sQuery(id+"F16.wireOp",EDGE,"E93.MirrorCS");Q0=makeQuery(id+"F16.imprint","IMPRINT",FACE,{"disambiguationData":[TD([[makeQuery(id+"F16.imprint","IMPRINT",EDGE,{"derivedFrom":subQ0}),1.0]])]});}
            var Q1;
            {var subQ1=sQuery(id+"F16.wireOp",EDGE,"E85");Q1=makeQuery(id+"F16.imprint","IMPRINT",FACE,{"disambiguationData":[TD([[makeQuery(id+"F16.imprint","IMPRINT",EDGE,{"derivedFrom":subQ1}),-1.0]])]});}
            var Q2;
            {var subQ5=sQuery(id+"F16.wireOp",EDGE,"E82.1");Q2=makeQuery(id+"F16.imprint","IMPRINT",FACE,{"disambiguationData":[TD([[makeQuery(id+"F16.imprint","IMPRINT",EDGE,{"derivedFrom":subQ5}),1.0]])]});}
            var Q3;
            Q3=makeQuery(id+"F2.opExtrude","CAP_FACE",FACE,{"disambiguationData":[OSD([sQuery(id+"F0.wireOp",EDGE,"E12"),sQuery(id+"F0.wireOp",EDGE,"E13"),sQuery(id+"F0.wireOp",EDGE,"E14"),sQuery(id+"F0.wireOp",EDGE,"E15"),sQuery(id+"F0.wireOp",EDGE,"E17.filletArc"),sQuery(id+"F0.wireOp",EDGE,"E18.filletArc"),sQuery(id+"F0.wireOp",EDGE,"E19.filletArc"),sQuery(id+"F0.wireOp",EDGE,"E20.filletArc"),sQuery(id+"F0.wireOp",EDGE,"E25.0"),sQuery(id+"F0.wireOp",EDGE,"E25.1"),sQuery(id+"F0.wireOp",EDGE,"E25.2"),sQuery(id+"F0.wireOp",EDGE,"E25.3"),sQuery(id+"F0.wireOp",EDGE,"E25.4"),sQuery(id+"F0.wireOp",EDGE,"E25.5"),sQuery(id+"F0.wireOp",EDGE,"E25.6"),sQuery(id+"F0.wireOp",EDGE,"E25.7")])],"isStart":false});
            extrude(context, id + "F17", {"entities" : qUnion([Q0, Q1, Q2]), "endBound" : BoundingType.UP_TO_SURFACE, "depth" : 25 * mm, "endBoundEntityFace" : qUnion([Q3]), "offsetDistance" : 25 * mm});
        }
    });
